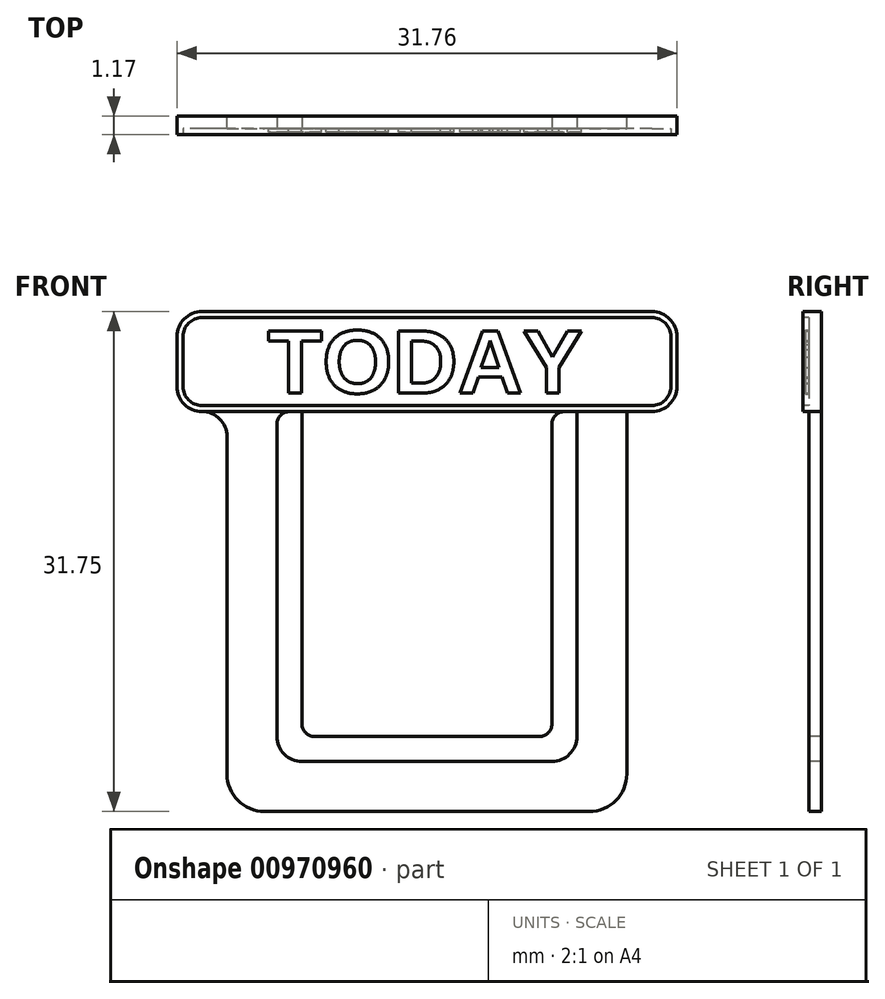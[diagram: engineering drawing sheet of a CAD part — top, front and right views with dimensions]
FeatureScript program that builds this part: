
annotation { "Feature Type Name" : "Feature", "Feature Type Description" : "" }
export const myFeature = defineFeature(function(context is Context, id is Id, definition is map)
    precondition{}
    {
        {
            var Q0;
            Q0=qCreatedBy(makeId("Front.planeOp"),FACE);
            var sketch = newSketch(context, id + "F0", { "sketchPlane" : qUnion([Q0])});
            skLineSegment(sketch, "E0.bottom", {"start": v(12.7, 12.7) * mm, "end": v(-12.7, 12.7) * mm});
            skLineSegment(sketch, "E0.top", {"start": v(12.7, -12.7) * mm, "end": v(-12.7, -12.7) * mm});
            skLineSegment(sketch, "E0.left", {"start": v(12.7, 12.7) * mm, "end": v(12.7, -12.7) * mm});
            skLineSegment(sketch, "E0.right", {"start": v(-12.7, 12.7) * mm, "end": v(-12.7, -12.7) * mm});
            skPoint(sketch, "E0.middle", {"position": v(0, 0) * mm});
            skSolve(sketch);
        }
        {
            var Q0;
            Q0=makeQuery(id+"F0.imprint","IMPRINT",FACE,{"disambiguationData":[TD([[makeQuery(id+"F0.imprint","IMPRINT",EDGE,{"derivedFrom":sQuery(id+"F0.wireOp",EDGE,"E0.bottom")}),1.0]])]});
            extrude(context, id + "F1", {"entities" : qUnion([Q0]), "depth" : 0.8 * mm, "offsetDistance" : 25.4 * mm});
        }
        {
            var Q0;
            Q0=makeQuery(id+"F1.opExtrude","SWEPT_EDGE",EDGE,{"disambiguationData":[OSD([sQuery(id+"F0.wireOp",EDGE,"E0.top"),sQuery(id+"F0.wireOp",EDGE,"E0.left")])]});
            var Q1;
            Q1=makeQuery(id+"F1.opExtrude","SWEPT_EDGE",EDGE,{"disambiguationData":[OSD([sQuery(id+"F0.wireOp",EDGE,"E0.top"),sQuery(id+"F0.wireOp",EDGE,"E0.right")])]});
            fillet(context, id + "F2", {"entities" : qUnion([Q0, Q1]), "radius" : 2.38 * mm, "tangentPropagation" : true, "allowEdgeOverflow" : false});
        }
        {
            var Q0;
            Q0=makeQuery(id+"F1.opExtrude","CAP_FACE",FACE,{"disambiguationData":[OSD([sQuery(id+"F0.wireOp",EDGE,"E0.bottom"),sQuery(id+"F0.wireOp",EDGE,"E0.top"),sQuery(id+"F0.wireOp",EDGE,"E0.left"),sQuery(id+"F0.wireOp",EDGE,"E0.right")])],"isStart":false});
            var sketch = newSketch(context, id + "F3", { "sketchPlane" : qUnion([Q0])});
            skLineSegment(sketch, "E1.bottom", {"start": v(9.52, 12.7) * mm, "end": v(-9.53, 12.7) * mm});
            skLineSegment(sketch, "E1.top", {"start": v(9.53, -9.53) * mm, "end": v(-9.52, -9.53) * mm});
            skLineSegment(sketch, "E1.left", {"start": v(9.52, 12.7) * mm, "end": v(9.53, -9.53) * mm});
            skLineSegment(sketch, "E1.right", {"start": v(-9.53, 12.7) * mm, "end": v(-9.52, -9.53) * mm});
            skPoint(sketch, "E1.middle", {"position": v(0, 0) * mm});
            skSolve(sketch);
        }
        {
            var Q0;
            Q0=makeQuery(id+"F3.imprint","IMPRINT",FACE,{"disambiguationData":[TD([[makeQuery(id+"F3.imprint","IMPRINT",EDGE,{"derivedFrom":sQuery(id+"F3.wireOp",EDGE,"E1.bottom")}),1.0]])]});
            extrude(context, id + "F4", {"entities" : qUnion([Q0]), "operationType" : NewBodyOperationType.REMOVE, "oppositeDirection" : true, "depth" : 4.93 * mm, "offsetDistance" : 25.4 * mm});
        }
        {
            var Q0;
            Q0=makeQuery(id+"F1.opExtrude","CAP_FACE",FACE,{"disambiguationData":[OSD([sQuery(id+"F0.wireOp",EDGE,"E0.bottom"),sQuery(id+"F0.wireOp",EDGE,"E0.top"),sQuery(id+"F0.wireOp",EDGE,"E0.left"),sQuery(id+"F0.wireOp",EDGE,"E0.right")])],"isStart":false});
            var sketch = newSketch(context, id + "F5", { "sketchPlane" : qUnion([Q0])});
            skLineSegment(sketch, "E2.bottom", {"start": v(-15.88, 12.7) * mm, "end": v(15.88, 12.7) * mm});
            skLineSegment(sketch, "E2.top", {"start": v(-15.88, 19.05) * mm, "end": v(15.88, 19.05) * mm});
            skLineSegment(sketch, "E2.left", {"start": v(-15.88, 12.7) * mm, "end": v(-15.88, 19.05) * mm});
            skLineSegment(sketch, "E2.right", {"start": v(15.87, 12.7) * mm, "end": v(15.87, 19.05) * mm});
            skSolve(sketch);
        }
        {
            var Q0;
            Q0=makeQuery(id+"F5.imprint","IMPRINT",FACE,{"disambiguationData":[TD([[makeQuery(id+"F5.imprint","IMPRINT",EDGE,{"derivedFrom":sQuery(id+"F5.wireOp",EDGE,"E2.top")}),-1.0]])]});
            extrude(context, id + "F6", {"entities" : qUnion([Q0]), "operationType" : NewBodyOperationType.ADD, "oppositeDirection" : true, "depth" : 0.8 * mm, "offsetDistance" : 25.4 * mm});
        }
        {
            var Q0;
            Q0=makeQuery(id+"F6.opExtrude","SWEPT_EDGE",EDGE,{"disambiguationData":[OSD([sQuery(id+"F5.wireOp",EDGE,"E2.top"),sQuery(id+"F5.wireOp",EDGE,"E2.left")])]});
            var Q1;
            Q1=makeQuery(id+"F6.opExtrude","SWEPT_EDGE",EDGE,{"disambiguationData":[OSD([sQuery(id+"F5.wireOp",EDGE,"E2.top"),sQuery(id+"F5.wireOp",EDGE,"E2.right")])]});
            var Q2;
            Q2=makeQuery(id+"F6.opExtrude","SWEPT_EDGE",EDGE,{"disambiguationData":[OSD([sQuery(id+"F5.wireOp",EDGE,"E2.bottom"),sQuery(id+"F5.wireOp",EDGE,"E2.right")])]});
            var Q3;
            Q3=makeQuery(id+"F1.opExtrude","SWEPT_EDGE",EDGE,{"disambiguationData":[OSD([sQuery(id+"F0.wireOp",EDGE,"E0.bottom"),sQuery(id+"F0.wireOp",EDGE,"E0.left")])]});
            var Q4;
            Q4=makeQuery(id+"F6.opExtrude","SWEPT_EDGE",EDGE,{"disambiguationData":[OSD([sQuery(id+"F5.wireOp",EDGE,"E2.bottom"),sQuery(id+"F5.wireOp",EDGE,"E2.left")])]});
            var Q5;
            Q5=makeQuery(id+"F1.opExtrude","SWEPT_EDGE",EDGE,{"disambiguationData":[OSD([sQuery(id+"F0.wireOp",EDGE,"E0.bottom"),sQuery(id+"F0.wireOp",EDGE,"E0.right")])]});
            fillet(context, id + "F7", {"entities" : qUnion([Q0, Q1, Q2, Q3, Q4, Q5]), "radius" : 1.59 * mm, "tangentPropagation" : true, "allowEdgeOverflow" : false});
        }
        {
            var Q0;
            Q0=makeQuery(id+"F4.boolean.opBoolean","COPY",EDGE,{"derivedFrom":makeQuery(id+"F4.opExtrude","SWEPT_EDGE",EDGE,{"disambiguationData":[OSD([sQuery(id+"F3.wireOp",EDGE,"E1.top"),sQuery(id+"F3.wireOp",EDGE,"E1.right")])]})});
            var Q1;
            Q1=makeQuery(id+"F4.boolean.opBoolean","COPY",EDGE,{"derivedFrom":makeQuery(id+"F4.opExtrude","SWEPT_EDGE",EDGE,{"disambiguationData":[OSD([sQuery(id+"F3.wireOp",EDGE,"E1.top"),sQuery(id+"F3.wireOp",EDGE,"E1.left")])]})});
            fillet(context, id + "F8", {"entities" : qUnion([Q0, Q1]), "radius" : 1.59 * mm, "tangentPropagation" : true, "allowEdgeOverflow" : false});
        }
        {
            var Q0;
            Q0=makeQuery(id+"F6.boolean.opBoolean","MERGE",FACE,{"derivedFrom":[makeQuery(id+"F1.opExtrude","CAP_FACE",FACE,{"disambiguationData":[OSD([sQuery(id+"F0.wireOp",EDGE,"E0.bottom"),sQuery(id+"F0.wireOp",EDGE,"E0.top"),sQuery(id+"F0.wireOp",EDGE,"E0.left"),sQuery(id+"F0.wireOp",EDGE,"E0.right")])],"isStart":false}),makeQuery(id+"F6.opExtrude","CAP_FACE",FACE,{"disambiguationData":[OSD([sQuery(id+"F5.wireOp",EDGE,"E2.bottom"),sQuery(id+"F5.wireOp",EDGE,"E2.top"),sQuery(id+"F5.wireOp",EDGE,"E2.left"),sQuery(id+"F5.wireOp",EDGE,"E2.right")])],"isStart":true})]});
            var sketch = newSketch(context, id + "F9", { "sketchPlane" : qUnion([Q0])});
            skLineSegment(sketch, "E3.bottom", {"start": v(-7.94, 12.7) * mm, "end": v(7.94, 12.7) * mm});
            skLineSegment(sketch, "E3.top", {"start": v(-7.94, -7.94) * mm, "end": v(7.94, -7.94) * mm});
            skLineSegment(sketch, "E3.left", {"start": v(-7.94, 12.7) * mm, "end": v(-7.94, -7.94) * mm});
            skLineSegment(sketch, "E3.right", {"start": v(7.94, 12.7) * mm, "end": v(7.94, -7.94) * mm});
            skSolve(sketch);
        }
        {
            var Q0;
            Q0=makeQuery(id+"F9.imprint","IMPRINT",FACE,{"disambiguationData":[TD([[makeQuery(id+"F9.imprint","IMPRINT",EDGE,{"derivedFrom":sQuery(id+"F9.wireOp",EDGE,"E3.bottom")}),1.0]])]});
            extrude(context, id + "F10", {"entities" : qUnion([Q0]), "operationType" : NewBodyOperationType.ADD, "oppositeDirection" : true, "depth" : 0.8 * mm, "offsetDistance" : 25.4 * mm});
        }
        {
            var Q0;
            Q0=makeQuery(id+"F10.opExtrude","SWEPT_EDGE",EDGE,{"disambiguationData":[OSD([sQuery(id+"F5.wireOp",EDGE,"E2.bottom"),sQuery(id+"F9.wireOp",EDGE,"E3.bottom"),sQuery(id+"F9.wireOp",EDGE,"E3.left")])]});
            var Q1;
            Q1=makeQuery(id+"F4.boolean.opBoolean","COPY",EDGE,{"derivedFrom":makeQuery(id+"F4.opExtrude","SWEPT_EDGE",EDGE,{"disambiguationData":[OSD([sQuery(id+"F0.wireOp",EDGE,"E0.bottom"),sQuery(id+"F3.wireOp",EDGE,"E1.bottom"),sQuery(id+"F3.wireOp",EDGE,"E1.right")])]})});
            var Q2;
            Q2=makeQuery(id+"F10.opExtrude","SWEPT_EDGE",EDGE,{"disambiguationData":[OSD([sQuery(id+"F5.wireOp",EDGE,"E2.bottom"),sQuery(id+"F9.wireOp",EDGE,"E3.bottom"),sQuery(id+"F9.wireOp",EDGE,"E3.right")])]});
            var Q3;
            Q3=makeQuery(id+"F4.boolean.opBoolean","COPY",EDGE,{"derivedFrom":makeQuery(id+"F4.opExtrude","SWEPT_EDGE",EDGE,{"disambiguationData":[OSD([sQuery(id+"F0.wireOp",EDGE,"E0.bottom"),sQuery(id+"F3.wireOp",EDGE,"E1.bottom"),sQuery(id+"F3.wireOp",EDGE,"E1.left")])]})});
            fillet(context, id + "F11", {"entities" : qUnion([Q0, Q1, Q2, Q3]), "radius" : 0.8 * mm, "tangentPropagation" : true, "allowEdgeOverflow" : false});
        }
        {
            var Q0;
            Q0=makeQuery(id+"F10.opExtrude","SWEPT_EDGE",EDGE,{"disambiguationData":[OSD([sQuery(id+"F9.wireOp",EDGE,"E3.top"),sQuery(id+"F9.wireOp",EDGE,"E3.left")])]});
            var Q1;
            Q1=makeQuery(id+"F10.opExtrude","SWEPT_EDGE",EDGE,{"disambiguationData":[OSD([sQuery(id+"F9.wireOp",EDGE,"E3.top"),sQuery(id+"F9.wireOp",EDGE,"E3.right")])]});
            fillet(context, id + "F12", {"entities" : qUnion([Q0, Q1]), "radius" : 0.8 * mm, "tangentPropagation" : true, "allowEdgeOverflow" : false});
        }
        {
            var Q0;
            Q0=makeQuery(id+"F10.boolean.opBoolean","MERGE",FACE,{"derivedFrom":[makeQuery(id+"F6.boolean.opBoolean","MERGE",FACE,{"derivedFrom":[makeQuery(id+"F1.opExtrude","CAP_FACE",FACE,{"disambiguationData":[OSD([sQuery(id+"F0.wireOp",EDGE,"E0.bottom"),sQuery(id+"F0.wireOp",EDGE,"E0.top"),sQuery(id+"F0.wireOp",EDGE,"E0.left"),sQuery(id+"F0.wireOp",EDGE,"E0.right")])],"isStart":false}),makeQuery(id+"F6.opExtrude","CAP_FACE",FACE,{"disambiguationData":[OSD([sQuery(id+"F5.wireOp",EDGE,"E2.bottom"),sQuery(id+"F5.wireOp",EDGE,"E2.top"),sQuery(id+"F5.wireOp",EDGE,"E2.left"),sQuery(id+"F5.wireOp",EDGE,"E2.right")])],"isStart":true})]}),makeQuery(id+"F10.opExtrude","CAP_FACE",FACE,{"disambiguationData":[OSD([sQuery(id+"F9.wireOp",EDGE,"E3.bottom"),sQuery(id+"F9.wireOp",EDGE,"E3.top"),sQuery(id+"F9.wireOp",EDGE,"E3.left"),sQuery(id+"F9.wireOp",EDGE,"E3.right")])],"isStart":true})]});
            var sketch = newSketch(context, id + "F13", { "sketchPlane" : qUnion([Q0])});
            skArc(sketch, "E4.0", {"start": v(-14.29, 19.05) * mm, "mid": v(-15.41, 18.59) * mm, "end": v(-15.88, 17.46) * mm});
            skLineSegment(sketch, "E5.0", {"start": v(-15.88, 14.29) * mm, "end": v(-15.88, 17.46) * mm});
            skArc(sketch, "E6.0", {"start": v(-15.88, 14.29) * mm, "mid": v(-15.41, 13.16) * mm, "end": v(-14.29, 12.7) * mm});
            skLineSegment(sketch, "E7.0", {"start": v(-14.29, 19.05) * mm, "end": v(14.29, 19.05) * mm});
            skArc(sketch, "E8.0", {"start": v(15.87, 17.46) * mm, "mid": v(15.41, 18.59) * mm, "end": v(14.29, 19.05) * mm});
            skLineSegment(sketch, "E9.0", {"start": v(15.87, 14.29) * mm, "end": v(15.87, 17.46) * mm});
            skArc(sketch, "E10.0", {"start": v(14.29, 12.7) * mm, "mid": v(15.41, 13.16) * mm, "end": v(15.87, 14.29) * mm});
            skLineSegment(sketch, "E11", {"start": v(-14.29, 12.7) * mm, "end": v(14.29, 12.7) * mm});
            skSolve(sketch);
        }
        {
            var Q0;
            Q0=makeQuery(id+"F13.imprint","IMPRINT",FACE,{"disambiguationData":[TD([[makeQuery(id+"F13.imprint","IMPRINT",EDGE,{"derivedFrom":sQuery(id+"F13.wireOp",EDGE,"E4.0")}),1.0]])]});
            extrude(context, id + "F14", {"entities" : qUnion([Q0]), "operationType" : NewBodyOperationType.ADD, "depth" : 0.38 * mm, "offsetDistance" : 25.4 * mm});
        }
        {
            var Q0;
            Q0=makeQuery(id+"F14.opExtrude","CAP_FACE",FACE,{"disambiguationData":[OSD([sQuery(id+"F13.wireOp",EDGE,"E4.0"),sQuery(id+"F13.wireOp",EDGE,"E5.0"),sQuery(id+"F13.wireOp",EDGE,"E6.0"),sQuery(id+"F13.wireOp",EDGE,"E7.0"),sQuery(id+"F13.wireOp",EDGE,"E8.0"),sQuery(id+"F13.wireOp",EDGE,"E9.0"),sQuery(id+"F13.wireOp",EDGE,"E10.0"),sQuery(id+"F13.wireOp",EDGE,"E11")])],"isStart":false});
            var sketch = newSketch(context, id + "F15", { "sketchPlane" : qUnion([Q0])});
            skArc(sketch, "E12.0", {"start": v(-14.29, 19.05) * mm, "mid": v(-15.41, 18.59) * mm, "end": v(-15.88, 17.46) * mm});
            skLineSegment(sketch, "E13.0", {"start": v(-14.29, 19.05) * mm, "end": v(14.29, 19.05) * mm});
            skLineSegment(sketch, "E14.0", {"start": v(-15.88, 14.29) * mm, "end": v(-15.88, 17.46) * mm});
            skArc(sketch, "E15.0", {"start": v(-15.88, 14.29) * mm, "mid": v(-15.41, 13.16) * mm, "end": v(-14.29, 12.7) * mm});
            skLineSegment(sketch, "E16.0", {"start": v(-14.29, 12.7) * mm, "end": v(14.29, 12.7) * mm});
            skArc(sketch, "E17.0", {"start": v(14.29, 12.7) * mm, "mid": v(15.41, 13.16) * mm, "end": v(15.87, 14.29) * mm});
            skArc(sketch, "E18.0", {"start": v(15.87, 17.46) * mm, "mid": v(15.41, 18.59) * mm, "end": v(14.29, 19.05) * mm});
            skArc(sketch, "E19", {"start": v(-14.29, 18.67) * mm, "mid": v(-15.14, 18.32) * mm, "end": v(-15.5, 17.46) * mm});
            skArc(sketch, "E20", {"start": v(-15.5, 14.29) * mm, "mid": v(-15.14, 13.43) * mm, "end": v(-14.29, 13.08) * mm});
            skArc(sketch, "E21", {"start": v(15.5, 17.46) * mm, "mid": v(15.14, 18.32) * mm, "end": v(14.29, 18.67) * mm});
            skArc(sketch, "E22", {"start": v(14.29, 13.08) * mm, "mid": v(15.14, 13.43) * mm, "end": v(15.5, 14.29) * mm});
            skLineSegment(sketch, "E23", {"start": v(-14.29, 19.05) * mm, "end": v(-14.29, 12.7) * mm, "construction": true});
            skLineSegment(sketch, "E24", {"start": v(-15.88, 17.46) * mm, "end": v(15.87, 17.46) * mm, "construction": true});
            skLineSegment(sketch, "E25", {"start": v(14.29, 19.05) * mm, "end": v(14.29, 12.7) * mm, "construction": true});
            skLineSegment(sketch, "E26", {"start": v(15.87, 14.29) * mm, "end": v(-15.88, 14.29) * mm, "construction": true});
            skLineSegment(sketch, "E27", {"start": v(14.29, 18.67) * mm, "end": v(-14.29, 18.67) * mm});
            skLineSegment(sketch, "E28", {"start": v(-15.5, 17.46) * mm, "end": v(-15.5, 14.29) * mm});
            skLineSegment(sketch, "E29", {"start": v(-14.29, 13.08) * mm, "end": v(14.29, 13.08) * mm});
            skLineSegment(sketch, "E30", {"start": v(15.5, 17.46) * mm, "end": v(15.5, 14.29) * mm});
            skSolve(sketch);
        }
        {
            var Q0;
            Q0=makeQuery(id+"F15.imprint","IMPRINT",FACE,{"disambiguationData":[TD([[makeQuery(id+"F15.imprint","IMPRINT",EDGE,{"derivedFrom":sQuery(id+"F15.wireOp",EDGE,"E19")}),1.0]])]});
            var Q1;
            {var subQ0=sQuery(id+"F9.wireOp",EDGE,"E3.right");var subQ1=sQuery(id+"F9.wireOp",EDGE,"E3.top");var subQ3=sQuery(id+"F0.wireOp",EDGE,"E0.bottom");var subQ4=sQuery(id+"F9.wireOp",EDGE,"E3.left");var subQ5=makeQuery(id+"F6.opExtrude","CAP_FACE",FACE,{"disambiguationData":[OSD([sQuery(id+"F5.wireOp",EDGE,"E2.bottom"),sQuery(id+"F5.wireOp",EDGE,"E2.top"),sQuery(id+"F5.wireOp",EDGE,"E2.left"),sQuery(id+"F5.wireOp",EDGE,"E2.right")])],"isStart":true});var subQ6=makeQuery(id+"F1.opExtrude","CAP_FACE",FACE,{"disambiguationData":[OSD([subQ3,sQuery(id+"F0.wireOp",EDGE,"E0.top"),sQuery(id+"F0.wireOp",EDGE,"E0.left"),sQuery(id+"F0.wireOp",EDGE,"E0.right")])],"isStart":false});var subQ7=makeQuery(id+"F10.opExtrude","CAP_FACE",FACE,{"disambiguationData":[OSD([sQuery(id+"F9.wireOp",EDGE,"E3.bottom"),subQ1,subQ4,subQ0])],"isStart":true});Q1=makeQuery(id+"F14.boolean.opBoolean","SPLIT",FACE,{"disambiguationData":[TD([makeQuery(id+"F10.opExtrude","SWEPT_FACE",FACE,{"disambiguationData":[OSD([subQ1])]})])],"derivedFrom":makeQuery(id+"F10.boolean.opBoolean","MERGE",FACE,{"derivedFrom":[makeQuery(id+"F6.boolean.opBoolean","MERGE",FACE,{"derivedFrom":[subQ6,subQ5]}),subQ7]})});}
            extrude(context, id + "F16", {"entities" : qUnion([Q0]), "operationType" : NewBodyOperationType.REMOVE, "endBound" : BoundingType.UP_TO_SURFACE, "oppositeDirection" : true, "depth" : 25.4 * mm, "endBoundEntityFace" : qUnion([Q1]), "offsetDistance" : 25.4 * mm});
        }
        {
            var Q0;
            Q0=qCreatedBy(makeId("Front.planeOp"),FACE);
            var sketch = newSketch(context, id + "F17", { "sketchPlane" : qUnion([Q0])});
            skText(sketch, "E31", { "text": "TODAY", "fontName": "Arimo-Bold.ttf"});
            const initialGuessF17  = {"E31": [-0.01013, 0.01388, 1, 0, 0.00412]};
            skSetInitialGuess(sketch, initialGuessF17);
            skSolve(sketch);
        }
        {
            var Q0;
            Q0=qSketchRegion(id+"F17",true);
            extrude(context, id + "F18", {"entities" : qUnion([Q0]), "operationType" : NewBodyOperationType.ADD, "depth" : 1.02 * mm, "offsetDistance" : 25.4 * mm});
        }
    });
